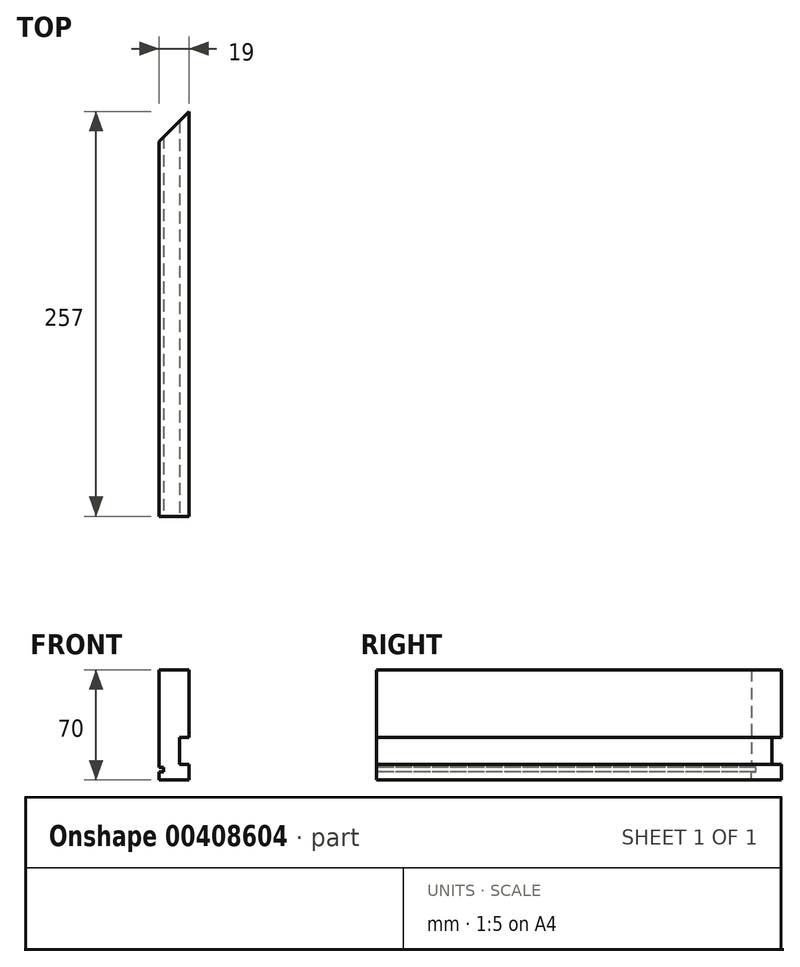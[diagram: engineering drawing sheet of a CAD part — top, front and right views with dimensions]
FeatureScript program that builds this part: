
annotation { "Feature Type Name" : "Feature", "Feature Type Description" : "" }
export const myFeature = defineFeature(function(context is Context, id is Id, definition is map)
    precondition{}
    {
        {
            var Q0;
            Q0=qCreatedBy(makeId("Right.planeOp"),FACE);
            var sketch = newSketch(context, id + "F0", { "sketchPlane" : qUnion([Q0])});
            skLineSegment(sketch, "E0.bottom", {"start": v(0, 0) * mm, "end": v(-257, 0) * mm});
            skLineSegment(sketch, "E0.top", {"start": v(0, 70) * mm, "end": v(-257, 70) * mm});
            skLineSegment(sketch, "E0.left", {"start": v(0, 0) * mm, "end": v(0, 70) * mm});
            skLineSegment(sketch, "E0.right", {"start": v(-257, 0) * mm, "end": v(-257, 70) * mm});
            skSolve(sketch);
        }
        {
            var Q0;
            Q0 = qSketchRegion(id + "F0", true);
            extrude(context, id + "F1", {"entities" : qUnion([Q0]), "depth" : 19 * mm});
        }
        {
            var Q0;
            Q0=makeQuery(id+"F1.opExtrude","SWEPT_FACE",FACE,{"disambiguationData":[OSD([sQuery(id+"F0.wireOp",EDGE,"E0.right")])]});
            var sketch = newSketch(context, id + "F2", { "sketchPlane" : qUnion([Q0])});
            skLineSegment(sketch, "E1.bottom", {"start": v(0, 5) * mm, "end": v(3, 5) * mm});
            skLineSegment(sketch, "E1.top", {"start": v(0, 8) * mm, "end": v(3, 8) * mm});
            skLineSegment(sketch, "E1.left", {"start": v(0, 5) * mm, "end": v(0, 8) * mm});
            skLineSegment(sketch, "E1.right", {"start": v(3, 5) * mm, "end": v(3, 8) * mm});
            skSolve(sketch);
        }
        {
            var Q0;
            Q0=makeQuery(id+"F2.imprint","IMPRINT",FACE,{"disambiguationData":[TD([[makeQuery(id+"F2.imprint","IMPRINT",EDGE,{"derivedFrom":sQuery(id+"F2.wireOp",EDGE,"E1.bottom")}),1.0]])]});
            extrude(context, id + "F3", {"entities" : qUnion([Q0]), "operationType" : NewBodyOperationType.REMOVE, "endBound" : BoundingType.THROUGH_ALL, "oppositeDirection" : true, "depth" : 25 * mm});
        }
        {
            var Q0;
            Q0=makeQuery(id+"F1.opExtrude","SWEPT_FACE",FACE,{"disambiguationData":[OSD([sQuery(id+"F0.wireOp",EDGE,"E0.right")])]});
            var sketch = newSketch(context, id + "F4", { "sketchPlane" : qUnion([Q0])});
            skLineSegment(sketch, "E2.bottom", {"start": v(19, 10) * mm, "end": v(13, 10) * mm});
            skLineSegment(sketch, "E2.top", {"start": v(19, 27) * mm, "end": v(13, 27) * mm});
            skLineSegment(sketch, "E2.left", {"start": v(19, 10) * mm, "end": v(19, 27) * mm});
            skLineSegment(sketch, "E2.right", {"start": v(13, 10) * mm, "end": v(13, 27) * mm});
            skSolve(sketch);
        }
        {
            var Q0;
            Q0 = qSketchRegion(id + "F4", true);
            extrude(context, id + "F5", {"entities" : qUnion([Q0]), "operationType" : NewBodyOperationType.REMOVE, "endBound" : BoundingType.THROUGH_ALL, "oppositeDirection" : true, "depth" : 25 * mm});
        }
        {
            var Q0;
            {var subQ0=sQuery(id+"F0.wireOp",EDGE,"E0.left");var subQ1=sQuery(id+"F0.wireOp",EDGE,"E0.top");Q0=makeQuery(id+"F3.boolean.opBoolean","SPLIT",EDGE,{"disambiguationData":[TD([makeQuery(id+"F1.opExtrude","SWEPT_FACE",FACE,{"disambiguationData":[OSD([subQ1])]})])],"derivedFrom":makeQuery(id+"F1.opExtrude","CAP_EDGE",EDGE,{"disambiguationData":[OSD([subQ0])],"isStart":true})});}
            chamfer(context, id + "F6", {"entities" : qUnion([Q0]), "width" : 19 * mm, "tangentPropagation" : true});
        }
    });
